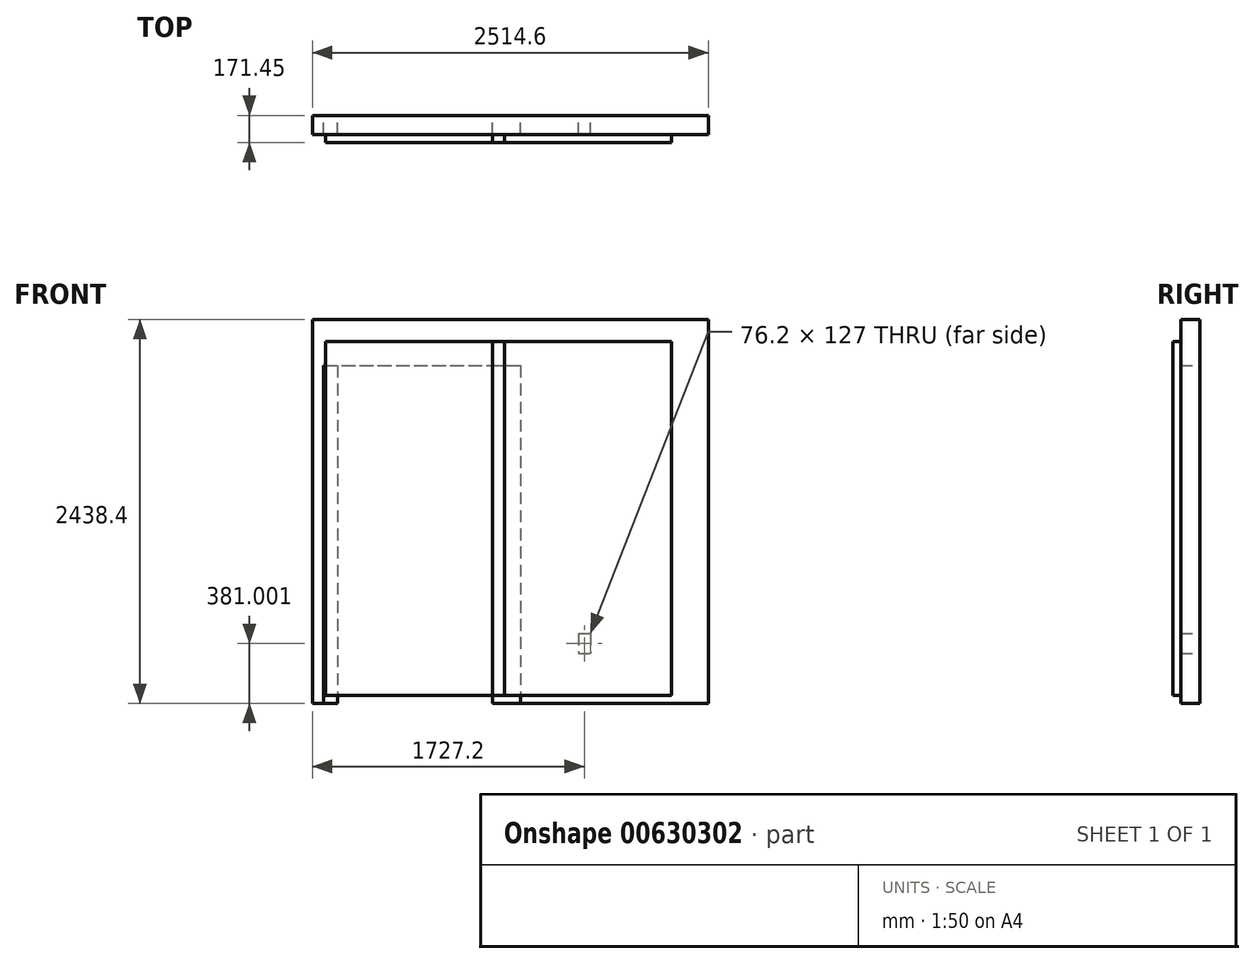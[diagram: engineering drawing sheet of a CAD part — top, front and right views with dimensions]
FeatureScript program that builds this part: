
annotation { "Feature Type Name" : "Feature", "Feature Type Description" : "" }
export const myFeature = defineFeature(function(context is Context, id is Id, definition is map)
    precondition{}
    {
        {
            var Q0;
            Q0=qCreatedBy(makeId("Front.planeOp"),FACE);
            var sketch = newSketch(context, id + "F0", { "sketchPlane" : qUnion([Q0])});
            skLineSegment(sketch, "E0.bottom", {"start": v(-1547.5, 1224.8) * mm, "end": v(967.1, 1224.8) * mm});
            skLineSegment(sketch, "E0.top", {"start": v(-1547.5, -1213.6) * mm, "end": v(-1477.66, -1213.6) * mm});
            skLineSegment(sketch, "E0.left", {"start": v(-1547.5, 1224.8) * mm, "end": v(-1547.5, -1213.6) * mm});
            skLineSegment(sketch, "E0.right", {"start": v(967.1, 1224.8) * mm, "end": v(967.1, -1213.6) * mm});
            skLineSegment(sketch, "E1.top", {"start": v(-1477.66, 932.7) * mm, "end": v(-226.7, 932.7) * mm});
            skLineSegment(sketch, "E1.left", {"start": v(-1477.66, -1213.6) * mm, "end": v(-1477.66, 932.7) * mm});
            skLineSegment(sketch, "E1.right", {"start": v(-226.7, -1213.6) * mm, "end": v(-226.7, 932.7) * mm});
            skLineSegment(sketch, "E2.trimOffspring", {"start": v(-226.7, -1213.6) * mm, "end": v(967.1, -1213.6) * mm});
            skLineSegment(sketch, "E3.bottom", {"start": v(141.6, -769.1) * mm, "end": v(217.8, -769.1) * mm});
            skLineSegment(sketch, "E3.top", {"start": v(141.6, -896.1) * mm, "end": v(217.8, -896.1) * mm});
            skLineSegment(sketch, "E3.left", {"start": v(141.6, -769.1) * mm, "end": v(141.6, -896.1) * mm});
            skLineSegment(sketch, "E3.right", {"start": v(217.8, -769.1) * mm, "end": v(217.8, -896.1) * mm});
            skSolve(sketch);
        }
        {
            var Q0;
            Q0 = qSketchRegion(id + "F0", true);
            extrude(context, id + "F1", {"entities" : qUnion([Q0]), "depth" : 120.65 * mm, "offsetDistance" : 25.4 * mm});
        }
        {
            var Q0;
            Q0=qCreatedBy(makeId("Front.planeOp"),FACE);
            var sketch = newSketch(context, id + "F2", { "sketchPlane" : qUnion([Q0])});
            skLineSegment(sketch, "E4.bottom", {"start": v(-1477.66, 932.7) * mm, "end": v(-1388.76, 932.7) * mm});
            skLineSegment(sketch, "E4.top", {"start": v(-1477.66, -1213.6) * mm, "end": v(-1388.76, -1213.6) * mm});
            skLineSegment(sketch, "E4.left", {"start": v(-1477.66, 932.7) * mm, "end": v(-1477.66, -1213.6) * mm});
            skLineSegment(sketch, "E4.right", {"start": v(-1388.76, 932.7) * mm, "end": v(-1388.76, -1213.6) * mm});
            skLineSegment(sketch, "E5.bottom", {"start": v(-404.5, 932.7) * mm, "end": v(-226.7, 932.7) * mm});
            skLineSegment(sketch, "E5.top", {"start": v(-404.5, -1213.6) * mm, "end": v(-226.7, -1213.6) * mm});
            skLineSegment(sketch, "E5.left", {"start": v(-404.5, 932.7) * mm, "end": v(-404.5, -1213.6) * mm});
            skLineSegment(sketch, "E5.right", {"start": v(-226.7, 932.7) * mm, "end": v(-226.7, -1213.6) * mm});
            skSolve(sketch);
        }
        {
            var Q0;
            Q0 = qSketchRegion(id + "F2", true);
            var Q1;
            Q1=makeQuery(id+"F1.opExtrude","CAP_FACE",FACE,{"disambiguationData":[OSD([sQuery(id+"F0.wireOp",EDGE,"E0.bottom"),sQuery(id+"F0.wireOp",EDGE,"E0.top"),sQuery(id+"F0.wireOp",EDGE,"E0.left"),sQuery(id+"F0.wireOp",EDGE,"E0.right"),sQuery(id+"F0.wireOp",EDGE,"E1.top"),sQuery(id+"F0.wireOp",EDGE,"E1.left"),sQuery(id+"F0.wireOp",EDGE,"E1.right"),sQuery(id+"F0.wireOp",EDGE,"E2.trimOffspring"),sQuery(id+"F0.wireOp",EDGE,"E3.bottom"),sQuery(id+"F0.wireOp",EDGE,"E3.top"),sQuery(id+"F0.wireOp",EDGE,"E3.left"),sQuery(id+"F0.wireOp",EDGE,"E3.right")])],"isStart":false});
            extrude(context, id + "F3", {"entities" : qUnion([Q0]), "endBound" : BoundingType.UP_TO_SURFACE, "depth" : 25.4 * mm, "endBoundEntityFace" : qUnion([Q1]), "offsetDistance" : 25.4 * mm});
        }
        {
            var Q0;
            Q0=makeQuery(id+"F1.opExtrude","CAP_FACE",FACE,{"disambiguationData":[OSD([sQuery(id+"F0.wireOp",EDGE,"E0.bottom"),sQuery(id+"F0.wireOp",EDGE,"E0.top"),sQuery(id+"F0.wireOp",EDGE,"E0.left"),sQuery(id+"F0.wireOp",EDGE,"E0.right"),sQuery(id+"F0.wireOp",EDGE,"E1.top"),sQuery(id+"F0.wireOp",EDGE,"E1.left"),sQuery(id+"F0.wireOp",EDGE,"E1.right"),sQuery(id+"F0.wireOp",EDGE,"E2.trimOffspring"),sQuery(id+"F0.wireOp",EDGE,"E3.bottom"),sQuery(id+"F0.wireOp",EDGE,"E3.top"),sQuery(id+"F0.wireOp",EDGE,"E3.left"),sQuery(id+"F0.wireOp",EDGE,"E3.right")])],"isStart":false});
            var sketch = newSketch(context, id + "F4", { "sketchPlane" : qUnion([Q0])});
            skLineSegment(sketch, "E6.bottom", {"start": v(-1464.96, 1085.1) * mm, "end": v(-328.3, 1085.1) * mm});
            skLineSegment(sketch, "E6.top", {"start": v(-1464.96, -1162.8) * mm, "end": v(-328.3, -1162.8) * mm});
            skLineSegment(sketch, "E6.left", {"start": v(-1464.96, 1085.1) * mm, "end": v(-1464.96, -1162.8) * mm});
            skLineSegment(sketch, "E6.right", {"start": v(-328.3, 1085.1) * mm, "end": v(-328.3, -1162.8) * mm});
            skSolve(sketch);
        }
        {
            var Q0;
            Q0 = qSketchRegion(id + "F4", true);
            extrude(context, id + "F5", {"entities" : qUnion([Q0]), "depth" : 50.8 * mm, "offsetDistance" : 25.4 * mm});
        }
        {
            var Q0;
            Q0=makeQuery(id+"F1.opExtrude","CAP_FACE",FACE,{"disambiguationData":[OSD([sQuery(id+"F0.wireOp",EDGE,"E0.bottom"),sQuery(id+"F0.wireOp",EDGE,"E0.top"),sQuery(id+"F0.wireOp",EDGE,"E0.left"),sQuery(id+"F0.wireOp",EDGE,"E0.right"),sQuery(id+"F0.wireOp",EDGE,"E1.top"),sQuery(id+"F0.wireOp",EDGE,"E1.left"),sQuery(id+"F0.wireOp",EDGE,"E1.right"),sQuery(id+"F0.wireOp",EDGE,"E2.trimOffspring"),sQuery(id+"F0.wireOp",EDGE,"E3.bottom"),sQuery(id+"F0.wireOp",EDGE,"E3.top"),sQuery(id+"F0.wireOp",EDGE,"E3.left"),sQuery(id+"F0.wireOp",EDGE,"E3.right")])],"isStart":false});
            var sketch = newSketch(context, id + "F6", { "sketchPlane" : qUnion([Q0])});
            skLineSegment(sketch, "E7.bottom", {"start": v(-404.5, 1085.1) * mm, "end": v(732.14, 1085.1) * mm});
            skLineSegment(sketch, "E7.top", {"start": v(-404.5, -1162.8) * mm, "end": v(732.14, -1162.8) * mm});
            skLineSegment(sketch, "E7.left", {"start": v(-404.5, 1085.1) * mm, "end": v(-404.5, -1162.8) * mm});
            skLineSegment(sketch, "E7.right", {"start": v(732.14, 1085.1) * mm, "end": v(732.14, -1162.8) * mm});
            skSolve(sketch);
        }
        {
            var Q0;
            Q0 = qSketchRegion(id + "F6", true);
            extrude(context, id + "F7", {"entities" : qUnion([Q0]), "depth" : 50.8 * mm, "offsetDistance" : 25.4 * mm});
        }
    });
